# Revit family: WVA-2.5-NPT
name_source: partatom
category: Mechanical Equipment
revit_build: Autodesk Revit MEP 2014 (Build: 20140709_2115(x64)
units: mm (PartAtom-declared; Revit-internal decimal feet)

## types (1)
- WVA-2.5-NPT
    A = 10"
    ApproximateShipmentWeight = 90 lbs
    ArrayRadius = 4 3/8"
    B = 23"
    BottomExtrusionHeight = 1/4"
    BottomRevolveHeight = 2 1/2"
    C = 10 1/2"
    CouplingHeight = 3 5/8"
    CylindarDia = 7"
    CylinderHalfLength = 5"
    CylinderHeight = 18"
    D = 11 1/2"
    Height1 = 3/4"
    Height2 = 1/8"
    HookDiameter = 1/4"
    HookDistance = 2"
    HookTopDistance = 3/8"
    HookWidth = 3/4"
    LeftHookDistance = 3/8"
    Manufacturer = Wessels Company
    MaximumFlow = 69 GPM
    MaximumOperatingPressure = 125 PSIG
    MaximumOperatingTemperature = 240°F
    Model = WVA-2-NPT
    NumberOfArray = 9
    PartNumber = 72080021
    PipeConnectionSize = 2"
    PipeConnectorDiameter = 2 1/2"
    PipeDiameter = 2 7/8"
    PipeNominalDiameter = 2 3/8"
    RevolveRadius = 3 1/2"
    RingDistance = 4 1/2"
    SideDrainExtrusion = 5/8"
    SideFlangeStep1 = 3 1/2"
    SideFlangeStep2 = 7 1/8"
    SideFlangeThickness = 7/8"
    SideFlangeThickness1 = 1/4"
    Step1Diameter = 1/2"
    Step2Diameter = 1 1/8"
    Step3Diameter = 1 7/8"
    Step4Diameter = 2 1/2"
    Step5Diameter = 2 1/8"
    TopExtrusionDiameter = 1 1/8"
    TotalHeight = 3 1/8"
    URL = http://westank.com

## geometry (parser evidence)
native form markers: Extrusion x3, Revolve x2, Sweep x5
no freeform markers — native parametric forms only
